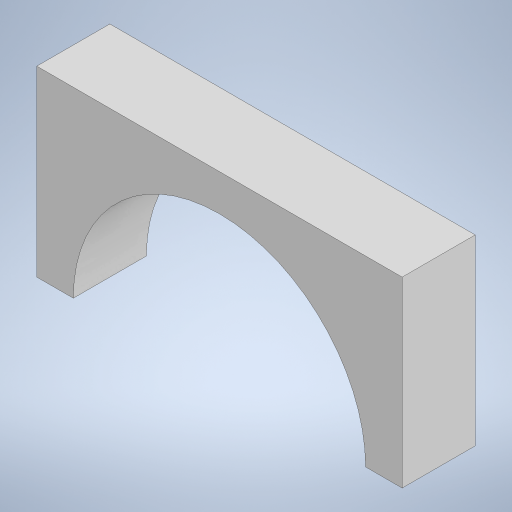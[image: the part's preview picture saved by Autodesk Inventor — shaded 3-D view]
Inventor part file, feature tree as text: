
AUTODESK INVENTOR PART (.ipt)
format: ipt  version: 2023 (Build 270158000, 158)  size: 240,128 bytes
history: native  units: mm
features: extrude x2, sketch x2
ambient origin geometry x8: Origin, YZ Plane, XZ Plane, XY Plane, X Axis, Y Axis, Z Axis, Center Point
bodies: Body1 (feature_tree)
feature tree (4):
  extrude  "Extrusion11"  Depth=50.0mm
  extrude  "Extrusion12"  Depth=20.0mm
  sketch  "Sketch13"  dims[d42=100.0mm d43=50.0mm]
  sketch  "Sketch14"  dims[d44=20.0mm d45=0.0mm d46=80.0mm d47=20.0mm d48=0.0mm]
